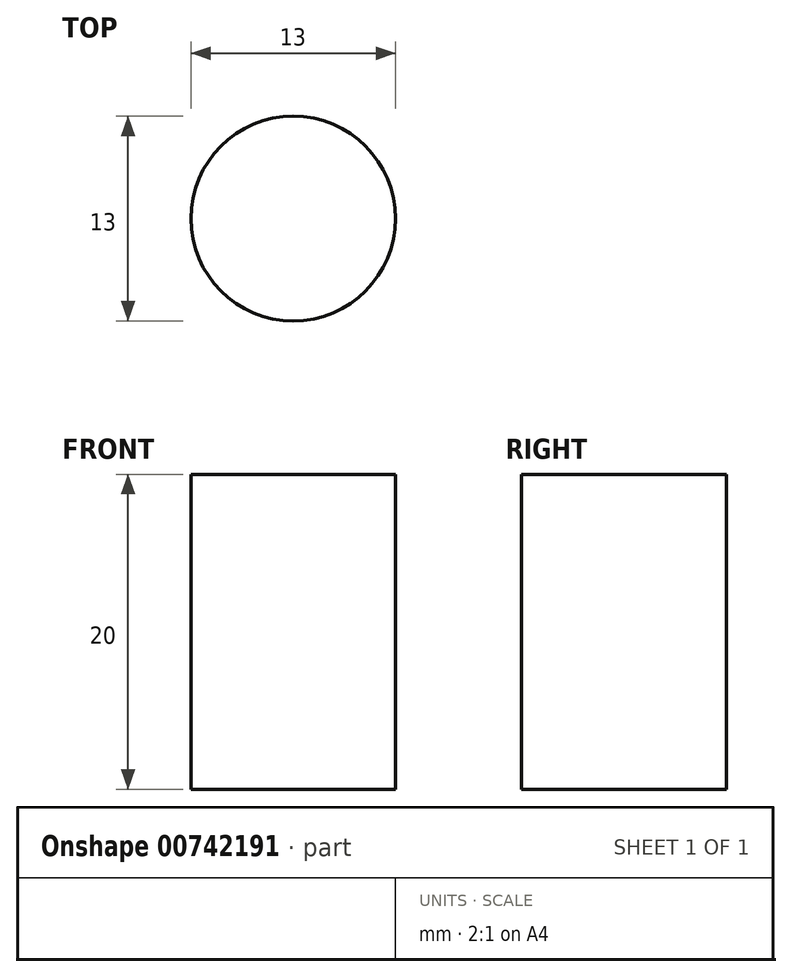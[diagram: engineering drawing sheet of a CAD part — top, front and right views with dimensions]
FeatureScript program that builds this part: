
annotation { "Feature Type Name" : "Feature", "Feature Type Description" : "" }
export const myFeature = defineFeature(function(context is Context, id is Id, definition is map)
    precondition{}
    {
        {
            var Q0;
            Q0=qCreatedBy(makeId("Front.planeOp"),FACE);
            var sketch = newSketch(context, id + "F0", { "sketchPlane" : qUnion([Q0])});
            skLineSegment(sketch, "E0.bottom", {"start": v(0, 0) * mm, "end": v(6.5, 0) * mm});
            skLineSegment(sketch, "E0.top", {"start": v(0, 20) * mm, "end": v(6.5, 20) * mm});
            skLineSegment(sketch, "E0.left", {"start": v(0, 0) * mm, "end": v(0, 20) * mm});
            skLineSegment(sketch, "E0.right", {"start": v(6.5, 0) * mm, "end": v(6.5, 20) * mm});
            skLineSegment(sketch, "E1", {"start": v(0, 0) * mm, "end": v(0, 29.37) * mm, "construction": true});
            skSolve(sketch);
        }
        {
            var Q0;
            Q0 = qSketchRegion(id + "F0", true);
            var Q1;
            Q1=sQuery(id+"F0.wireOp",EDGE,"E1");
            revolve(context, id + "F1", {"surfaceOperationType" : NewSurfaceOperationType.NEW, "entities" : qUnion([Q0]), "axis" : qUnion([Q1]), "revolveType" : RevolveType.FULL});
        }
    });
